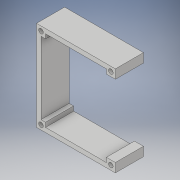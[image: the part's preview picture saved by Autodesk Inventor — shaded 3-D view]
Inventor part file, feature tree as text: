
AUTODESK INVENTOR PART (.ipt)
format: ipt  version: 2018 (Build 220112000, 112)  size: 136,704 bytes
history: native  units: in
note: dims shown in document units (in); Inventor stores cm internally (conversion verified against a paired STEP export)
features: extrude x2, sketch x2
ambient origin geometry x8: Origin, YZ Plane, XZ Plane, XY Plane, X Axis, Y Axis, Z Axis, Center Point
bodies: Solid1 (feature_tree)
feature tree (4):
  extrude  "Extrusion1"  Depth=3.5in
  extrude  "Extrusion2"  Depth=1.248in
  sketch  "Sketch1"  dims[d0=4.0in d1=3.5in]
  sketch  "Sketch2"  dims[d2=3.5in d3=5.0in d4=0.2in d5=0.2in d6=0.2031in d7=0.4in d8=0.4in d9=0.1in d10=1.248in d11=0.0in d12=1.248in d13=0.0in]
